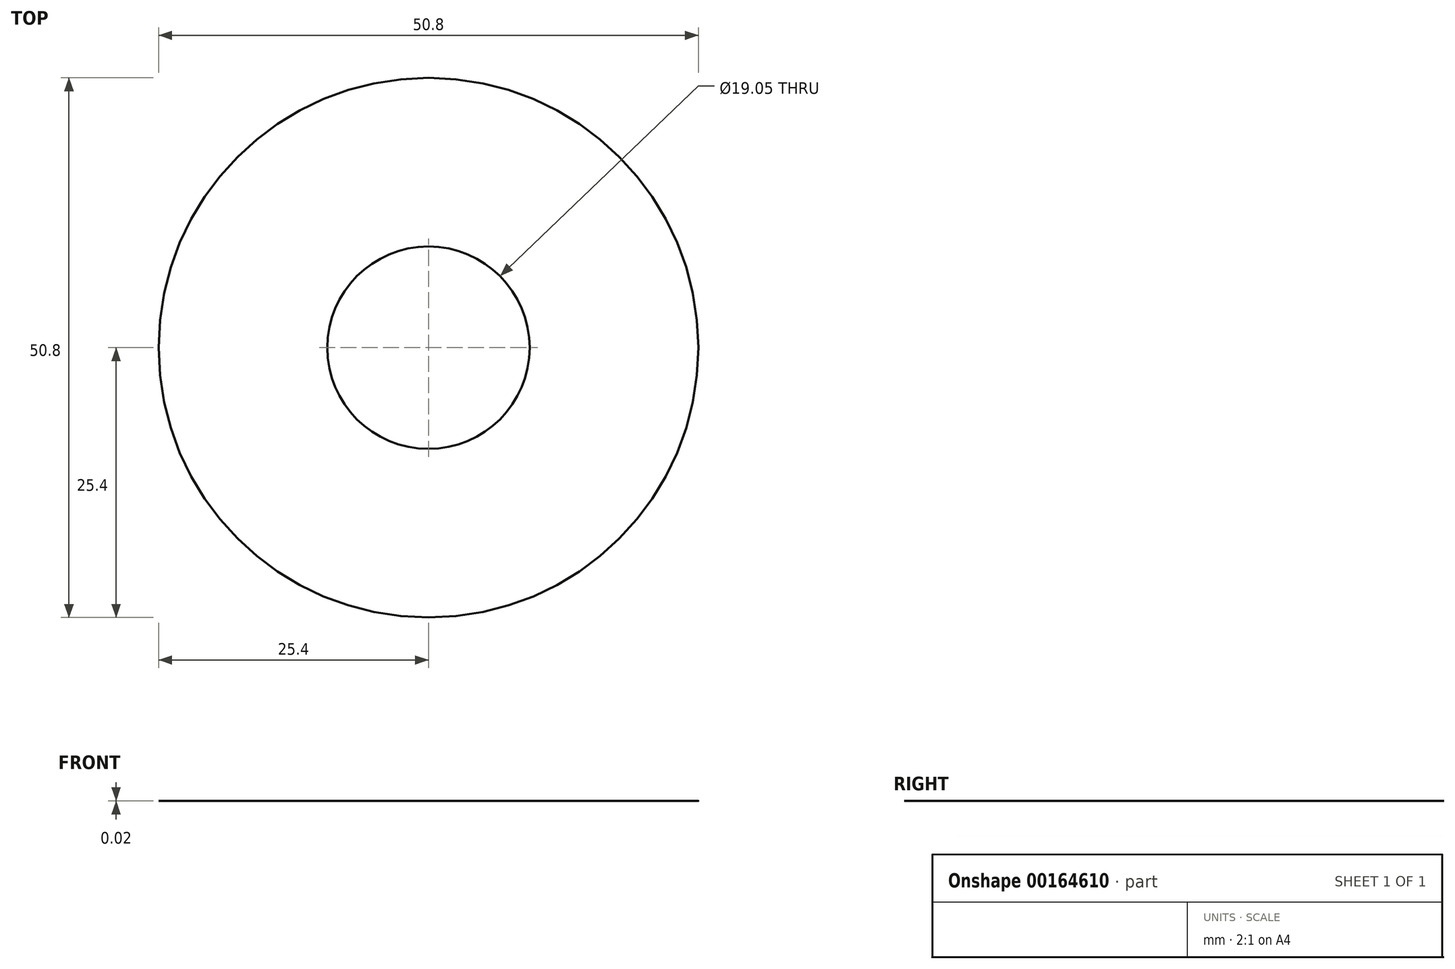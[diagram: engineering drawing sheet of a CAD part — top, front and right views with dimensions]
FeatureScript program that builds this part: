
annotation { "Feature Type Name" : "Feature", "Feature Type Description" : "" }
export const myFeature = defineFeature(function(context is Context, id is Id, definition is map)
    precondition{}
    {
        {
            var Q0;
            Q0=qCreatedBy(makeId("Top.planeOp"),FACE);
            var sketch = newSketch(context, id + "F0", { "sketchPlane" : qUnion([Q0])});
            skCircle(sketch, "E0", {"center": v(0, 0) * mm, "radius": 25.4 * mm});
            skCircle(sketch, "E1", {"center": v(0, 0) * mm, "radius": 9.53 * mm});
            skSolve(sketch);
        }
        {
            var Q0;
            Q0 = qSketchRegion(id + "F0", true);
            extrude(context, id + "F1", {"entities" : qUnion([Q0]), "depth" : 9 / 406.4 * mm});
        }
    });
